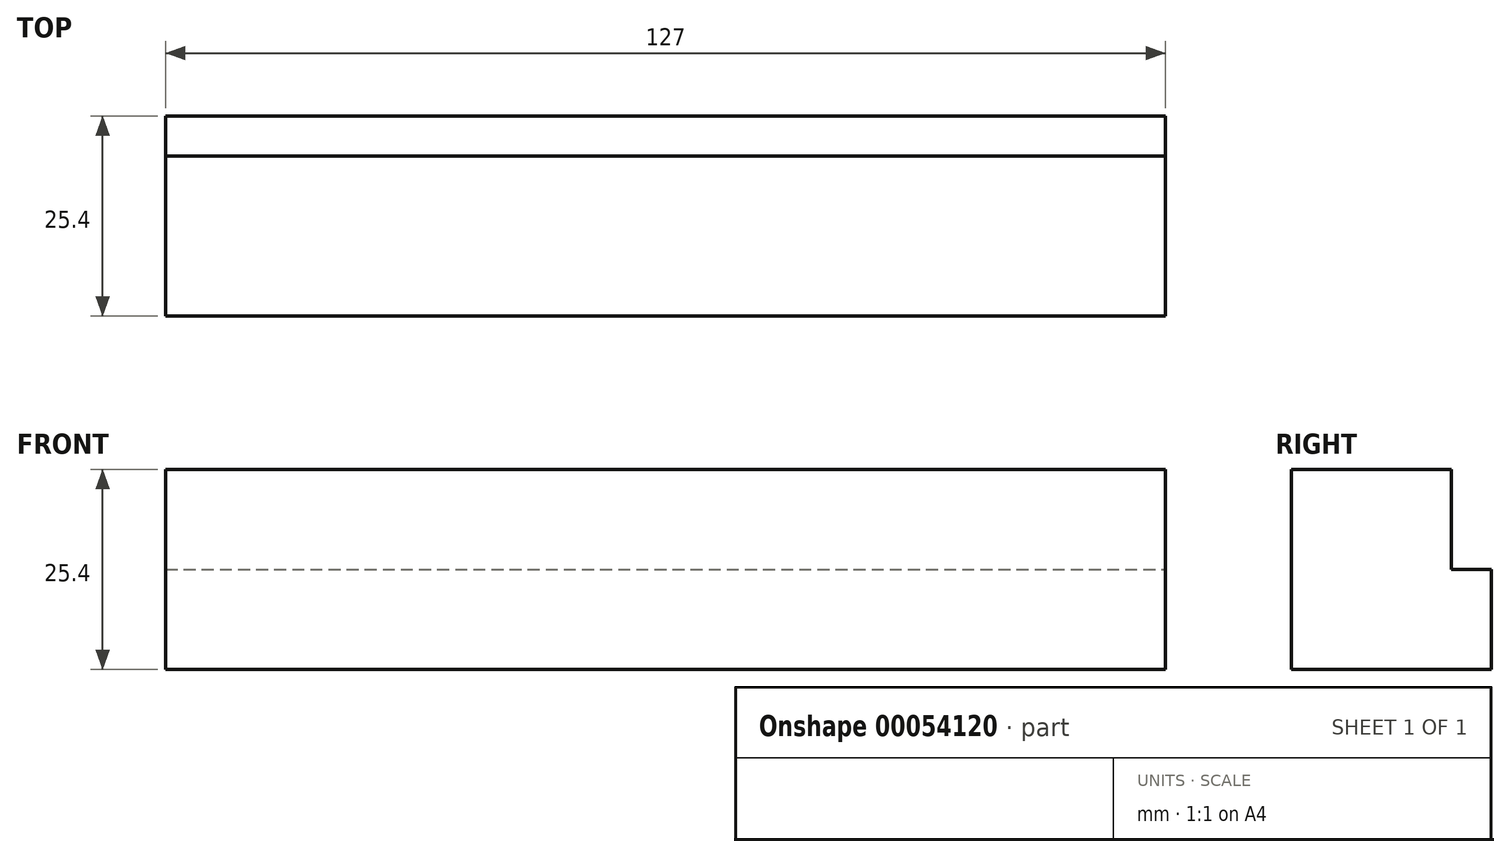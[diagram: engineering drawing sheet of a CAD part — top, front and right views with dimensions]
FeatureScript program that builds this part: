
annotation { "Feature Type Name" : "Feature", "Feature Type Description" : "" }
export const myFeature = defineFeature(function(context is Context, id is Id, definition is map)
    precondition{}
    {
        {
            var Q0;
            Q0=qCreatedBy(makeId("Right.planeOp"),FACE);
            var sketch = newSketch(context, id + "F0", { "sketchPlane" : qUnion([Q0])});
            skLineSegment(sketch, "E0.rect.bottom", {"start": v(-12.7, 12.7) * mm, "end": v(12.7, 12.7) * mm});
            skLineSegment(sketch, "E0.rect.top", {"start": v(-12.7, -12.7) * mm, "end": v(12.7, -12.7) * mm});
            skLineSegment(sketch, "E0.rect.left", {"start": v(-12.7, 12.7) * mm, "end": v(-12.7, -12.7) * mm});
            skLineSegment(sketch, "E0.rect.right", {"start": v(12.7, 12.7) * mm, "end": v(12.7, -12.7) * mm});
            skPoint(sketch, "E0.rect.middle", {"position": v(0, 0) * mm});
            skSolve(sketch);
        }
        {
            var Q0;
            Q0 = qSketchRegion(id + "F0", true);
            extrude(context, id + "F1", {"entities" : qUnion([Q0]), "endBound" : BoundingType.SYMMETRIC, "depth" : 127 * mm});
        }
        {
            var Q0;
            Q0=makeQuery(id+"F1.opExtrude","CAP_FACE",FACE,{"disambiguationData":[OSD([sQuery(id+"F0.wireOp",EDGE,"E0.rect.bottom"),sQuery(id+"F0.wireOp",EDGE,"E0.rect.top"),sQuery(id+"F0.wireOp",EDGE,"E0.rect.left"),sQuery(id+"F0.wireOp",EDGE,"E0.rect.right")])],"isStart":false});
            var sketch = newSketch(context, id + "F2", { "sketchPlane" : qUnion([Q0])});
            skLineSegment(sketch, "E1.bottom", {"start": v(12.7, 12.7) * mm, "end": v(7.62, 12.7) * mm});
            skLineSegment(sketch, "E1.top", {"start": v(12.7, 0) * mm, "end": v(7.62, 0) * mm});
            skLineSegment(sketch, "E1.left", {"start": v(12.7, 12.7) * mm, "end": v(12.7, 0) * mm});
            skLineSegment(sketch, "E1.right", {"start": v(7.62, 12.7) * mm, "end": v(7.62, 0) * mm});
            skSolve(sketch);
        }
        {
            var Q0;
            Q0 = qSketchRegion(id + "F2", true);
            extrude(context, id + "F3", {"entities" : qUnion([Q0]), "operationType" : NewBodyOperationType.REMOVE, "endBound" : BoundingType.THROUGH_ALL, "oppositeDirection" : true, "depth" : 25.4 * mm});
        }
    });
